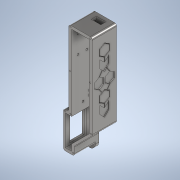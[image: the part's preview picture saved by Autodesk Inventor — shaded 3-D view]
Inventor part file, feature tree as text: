
AUTODESK INVENTOR PART (.ipt)
format: ipt  version: 2022 (Build 260153000, 153)  size: 702,464 bytes
history: native  units: in
note: dims shown in document units (in); Inventor stores cm internally (conversion verified against a paired STEP export)
features: extrude x19, sketch x18, projected_geometry x11, fillet x1
ambient origin geometry x8: Origin, YZ Plane, XZ Plane, XY Plane, X Axis, Y Axis, Z Axis, Center Point
bodies: Body1 (feature_tree)
feature tree (49):
  sketch  "Sketch1"  dims[d6=0.125in d8=135.0deg]
  extrude  "Extrusion2"  TaperAngle=135.0deg  [1 undecoded]
  extrude  "Extrusion3"  Depth=0.18in
  extrude  "Extrusion4"  Depth=0.18in
  extrude  "Extrusion6"  Depth=0.125in
  fillet  "Fillet1"  Radius=0.125in
  extrude  "Extrusion7"  Depth=1.3in TaperAngle=0.0deg
  extrude  "Extrusion8"  Depth=0.135in
  extrude  "Extrusion9"  Depth=0.06in
  sketch  "Sketch9"  dims[d72=0.06in d73=0.0in d81=0.185in]
  extrude  "Extrusion10"  Depth=0.06in TaperAngle=0.0deg
  extrude  "Extrusion11"  Depth=0.5in
  extrude  "Extrusion13"  Depth=0.06in TaperAngle=0.0deg
  extrude  "Extrusion14"  Depth=1.6in
  extrude  "Extrusion15"  TaperAngle=0.0deg  [1 undecoded]
  sketch  "Sketch16"  dims[d103=0.25in d104=0.0in d105=0.0in]
  extrude  "Extrusion16"  Depth=0.079in
  extrude  "Extrusion17"  Depth=0.079in
  extrude  "Extrusion18"  Depth=0.079in
  extrude  "Extrusion19"  Depth=0.079in
  extrude  "Extrusion20"  Depth=0.5in
  extrude  "Extrusion21"  Depth=0.4in
  extrude  "Extrusion22"  Depth=0.6in
  sketch  "Sketch2"  dims[d10=1.102in d17=0.18in]
  projected_geometry  "Projected Loop1"
  sketch  "Sketch4"  dims[d18=0.18in d21=0.18in]
  sketch  "Sketch5"  dims[d23=0.3937in d24=0.125in d27=0.125in d28=0.0in]
  sketch  "Sketch6"  dims[d29=0.125in d30=0.0in d31=1.3in d32=0.0in]
  sketch  "Sketch7"  dims[d35=0.125in d36=0.0in d37=0.135in]
  projected_geometry  "Projected Loop5"
  sketch  "Sketch10"  dims[d83=0.06in d84=0.0in d90=0.06in d91=0.0in]
  sketch  "Sketch11"  dims[d94=0.5in d97=0.079in]
  sketch  "Sketch13"  dims[d98=0.175in d99=0.06in d100=0.0in]
  projected_geometry  "Projected Loop7"
  sketch  "Sketch15"  dims[d101=0.9in d102=1.6in]
  projected_geometry  "Projected Loop8"
  projected_geometry  "Projected Loop9"
  sketch  "Sketch17"  dims[d114=0.079in d115=0.079in]
  projected_geometry  "Projected Loop10"
  sketch  "Sketch19"  dims[d116=0.079in d117=0.079in]
  projected_geometry  "Projected Loop12"
  sketch  "Sketch22"  dims[d118=0.079in d119=0.079in]
  sketch  "Sketch23"  dims[d120=0.079in d121=0.079in]
  projected_geometry  "Projected Loop13"
  sketch  "Sketch24"  dims[d122=0.5in d123=0.0in d124=0.12in]
  projected_geometry  "Projected Loop14"
  projected_geometry  "Projected Loop18"
  sketch  "Sketch27"  dims[d126=0.12in d128=0.4in d130=0.6in d132=1.0in d133=0.0in d134=0.4in d135=0.0in d136=0.548in d137=0.12in d138=0.12in d140=0.12in d141=2.702in d142=1.0in d143=0.0in d148=0.1in d149=0.0in d153=0.2559in d154=0.2559in d155=0.125in d156=0.35in d157=0.0in d158=0.225in d159=0.3in d160=0.325in d161=0.6in d162=0.35in d163=0.0in d164=1.3in d165=0.0in d166=1.0in d167=0.0in d168=0.13in d171=1.525in d172=0.763in d173=0.04in d174=0.04in d176=0.1in d177=1.525in d178=0.763in d193=0.068in d194=0.04in d195=0.04in d196=0.485in d197=0.1in d198=0.04in d199=0.1in d204=0.06in d205=0.0in d206=0.02in d207=0.02in d208=0.02in d209=0.02in d210=0.02in d202=0.5in d203=0.0344in]
  projected_geometry  "Projected Loop19"
note: 2 required parameter values undecoded (feature->parameter linkage not recoverable at this tier; creation-order binding heuristic only, values carry confidence <= 0.55)
